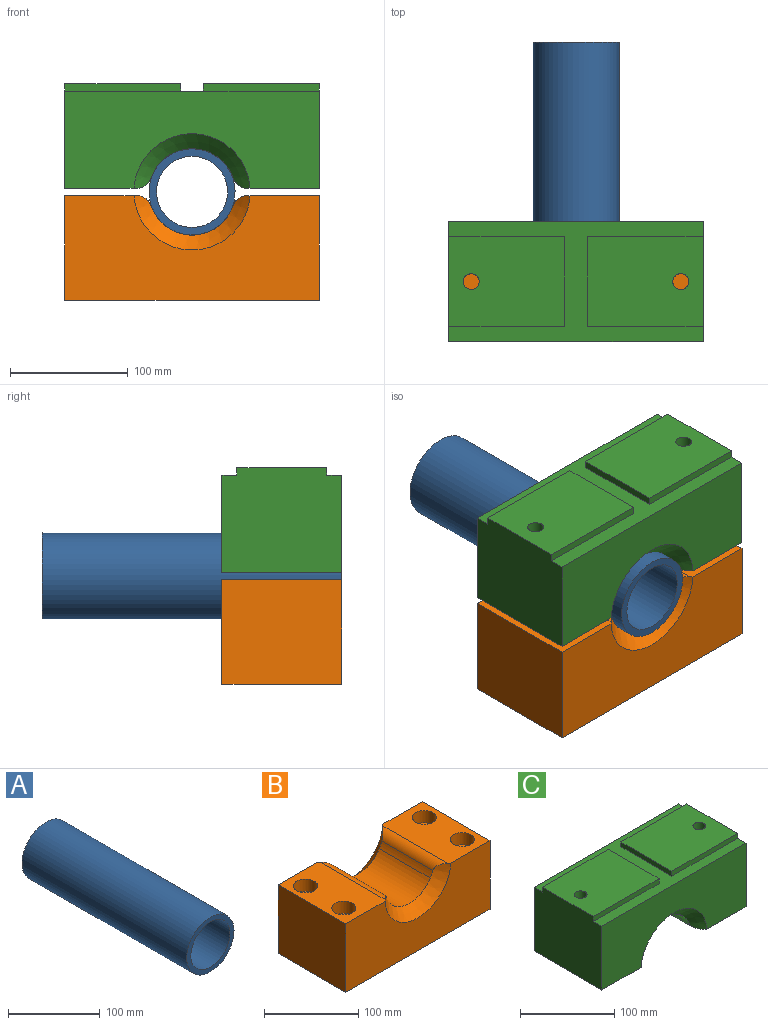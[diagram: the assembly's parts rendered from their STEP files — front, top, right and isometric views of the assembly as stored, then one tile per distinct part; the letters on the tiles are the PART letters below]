
ASSEMBLY  parts=3 mates=2
PART A: 4 faces, bbox 73x254x73 mm
  f0: cylinder r=30.16mm len=254mm, axis (0,1,0), area 48137.2mm2, adj f2,f3
  f1: cylinder r=36.51mm len=254mm, axis (0,1,0), area 58271.4mm2, adj f2,f3
  f2: plane 73.03x73.03mm, normal (0,-1,0), area 1330.1mm2, adj f0,f1
  f3: plane 73.03x73.03mm, normal (0,1,0), area 1330.1mm2, adj f0,f1
PART B: 26 faces, bbox 215.9x101.6x89.7 mm
  f0: plane 101.6x61.02mm, normal (0,0,1), area 5180.6mm2, adj f1,f3,f4,f10,f11,f12,f22,f25
  f1: plane 215.9x88.9mm, normal (0,-1,0), area 15680.8mm2, adj f0,f2,f3,f5,f6,f11
  f2: plane 101.6x88.9mm, normal (-1,0,0), area 9032.2mm2, adj f1,f4,f5,f6
  f3: plane 101.6x88.9mm, normal (1,0,0), area 9032.2mm2, adj f0,f1,f4,f6
  f4: plane 215.9x88.9mm, normal (0,1,0), area 15680.8mm2, adj f0,f2,f3,f5,f6,f10
  f5: plane 101.6x61.02mm, normal (0,0,1), area 5180.6mm2, adj f1,f2,f4,f10,f11,f13,f16,f19
  f6: plane 215.9x101.6mm, normal (0,0,-1), area 21363.5mm2, adj f1,f2,f3,f4,f14,f17,f20,f23
  f7: cylinder r=43.18mm len=76.6mm, axis (0,-1,0), area 694.4mm2, adj f8,f10,f11,f13
  f8: cylinder r=36.65mm len=76.2mm, axis (0,-1,0), area 5627.8mm2, adj f7,f9,f10,f11
  f9: cylinder r=43.18mm len=76.6mm, axis (0,-1,0), area 694.4mm2, adj f8,f10,f11,f12
  f10: cone r=36.65mm half-angle=45deg, axis (0,1,0), area 2253.2mm2, adj f0,f4,f5,f7,f8,f9,f12,f13
  f11: cone r=36.65mm half-angle=45deg, axis (0,-1,0), area 2253.2mm2, adj f0,f1,f5,f7,f8,f9,f12,f13
  f12: cylinder r=12.7mm len=96.97mm, axis (0,-1,0), area 1300.1mm2, adj f0,f9,f10,f11
  f13: cylinder r=12.7mm len=96.97mm, axis (0,-1,0), area 1300.1mm2, adj f5,f7,f10,f11
  f14: cylinder r=6.75mm len=73.03mm, axis (0,0,1), area 3095.4mm2, adj f6,f15
  f15: plane 25.4x25.4mm, normal (0,0,1), area 363.7mm2, adj f14,f16
  f16: cylinder r=12.7mm len=25.4mm, axis (0,0,1), area 1266.8mm2, adj f5,f15
  f17: cylinder r=6.75mm len=73.03mm, axis (0,0,1), area 3095.4mm2, adj f6,f18
  f18: plane 25.4x25.4mm, normal (0,0,1), area 363.7mm2, adj f17,f19
  f19: cylinder r=12.7mm len=25.4mm, axis (0,0,1), area 1266.8mm2, adj f5,f18
  f20: cylinder r=6.75mm len=73.03mm, axis (0,0,1), area 3095.4mm2, adj f6,f21
  f21: plane 25.4x25.4mm, normal (0,0,1), area 363.7mm2, adj f20,f22
  f22: cylinder r=12.7mm len=25.4mm, axis (0,0,1), area 1266.8mm2, adj f0,f21
  f23: cylinder r=6.75mm len=73.03mm, axis (0,0,1), area 3095.4mm2, adj f6,f24
  f24: plane 25.4x25.4mm, normal (0,0,1), area 363.7mm2, adj f23,f25
  f25: cylinder r=12.7mm len=25.4mm, axis (0,0,1), area 1266.8mm2, adj f0,f24
PART C: 26 faces, bbox 215.9x101.6x89.7 mm
  f0: plane 215.9x82.55mm, normal (0,-1,0), area 14294mm2, adj f2,f3,f6,f7,f12,f23
  f1: plane 215.9x82.55mm, normal (0,1,0), area 14294mm2, adj f2,f3,f6,f7,f11,f23
  f2: plane 101.6x88.9mm, normal (-1,0,0), area 8871mm2, adj f0,f1,f5,f7,f17,f21,f23
  f3: plane 101.6x88.9mm, normal (1,0,0), area 8870.9mm2, adj f0,f1,f4,f6,f18,f20,f23
  f4: plane 98.43x76.2mm, normal (0,0,1), area 7357mm2, adj f3,f18,f19,f20,f25
  f5: plane 98.43x76.2mm, normal (0,0,1), area 7357mm2, adj f2,f17,f21,f22,f24
  f6: plane 101.6x60.82mm, normal (0,0,-1), area 6031.5mm2, adj f0,f1,f3,f11,f12,f14,f25
  f7: plane 101.6x61.03mm, normal (0,0,-1), area 6052.1mm2, adj f0,f1,f2,f11,f12,f13,f24
  f8: cylinder r=43.18mm len=76.68mm, axis (0,-1,0), area 720.1mm2, adj f11,f12,f14,f16
  f9: cylinder r=36.65mm len=76.2mm, axis (0,-1,0), area 5622.8mm2, adj f11,f12,f15,f16
  f10: cylinder r=43.18mm len=76.68mm, axis (0,-1,0), area 691mm2, adj f11,f12,f13,f15
  f11: cone r=36.65mm half-angle=45deg, axis (0,1,0), area 2257mm2, adj f1,f6,f7,f8,f9,f10,f13,f14
  f12: cone r=36.65mm half-angle=45deg, axis (0,-1,0), area 2257mm2, adj f0,f6,f7,f8,f9,f10,f13,f14
  f13: cylinder r=12.7mm len=97.14mm, axis (0,-1,0), area 1302.6mm2, adj f7,f10,f11,f12
  f14: cylinder r=12.7mm len=97.14mm, axis (0,-1,0), area 1302.8mm2, adj f6,f8,f11,f12
  f15: cylinder r=12.7mm len=76.2mm, axis (0,-1,0), area 5.8mm2, adj f9,f10,f11,f12
  f16: cylinder r=12.7mm len=76.2mm, axis (0,-1,0), area 4.5mm2, adj f8,f9,f11,f12
  f17: plane 98.43x6.35mm, normal (0,-1,0), area 625mm2, adj f2,f5,f22,f23
  f18: plane 98.43x6.35mm, normal (0,-1,0), area 625mm2, adj f3,f4,f19,f23
  f19: plane 76.2x6.35mm, normal (-1,0,0), area 483.9mm2, adj f4,f18,f20,f23
  f20: plane 98.43x6.35mm, normal (0,1,0), area 625mm2, adj f3,f4,f19,f23
  f21: plane 98.43x6.35mm, normal (0,1,0), area 625mm2, adj f2,f5,f22,f23
  f22: plane 76.2x6.35mm, normal (1,0,0), area 483.9mm2, adj f5,f17,f21,f23
  f23: plane 215.9x101.6mm, normal (0,0,1), area 6935.5mm2, adj f0,f1,f2,f3,f17,f18,f19,f20
  f24: cylinder r=6.75mm len=88.9mm, axis (0,0,1), area 3768.3mm2, adj f5,f7
  f25: cylinder r=6.75mm len=88.9mm, axis (0,0,1), area 3768.3mm2, adj f4,f6
PLACE A t=(25.4,76.58,-102.56)mm
PLACE B t=(-82.55,-177.42,-194.63)mm fixed
PLACE C t=(-82.65,-177.42,-99.54)mm
MATE cylindrical A.f1 <-> B.f8  axis (0,1,0) through (25.4,-177.42,-102.56)mm
MATE cylindrical C.f9 <-> A.f1  axis (0,-1,0) through (25.4,-177.42,-102.56)mm
